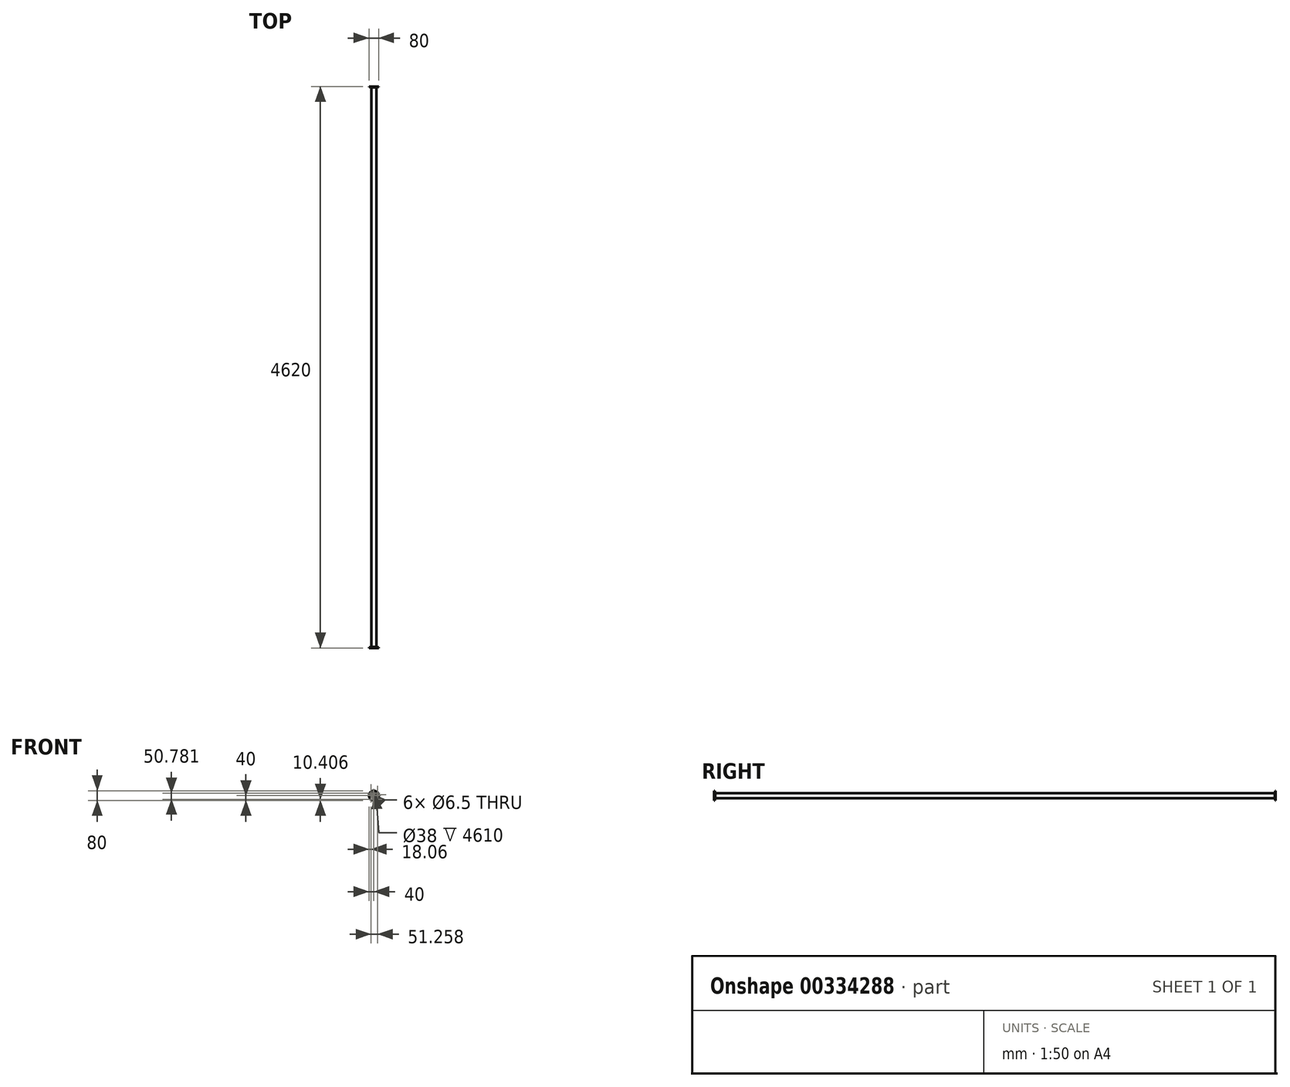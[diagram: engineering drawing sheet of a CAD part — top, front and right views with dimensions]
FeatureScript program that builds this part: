
annotation { "Feature Type Name" : "Feature", "Feature Type Description" : "" }
export const myFeature = defineFeature(function(context is Context, id is Id, definition is map)
    precondition{}
    {
        {
            assignVariable(context, id + "F0", {"name" : "L", "anyValue" : 4620});
        }
        {
            assignVariable(context, id + "F1", {"name" : "Dicke", "anyValue" : 5});
        }
        {
            var Q0;
            Q0=qCreatedBy(makeId("Front.planeOp"),FACE);
            var sketch = newSketch(context, id + "F2", { "sketchPlane" : qUnion([Q0])});
            skCircle(sketch, "E0", {"center": v(0, 0) * mm, "radius": 21 * mm});
            skCircle(sketch, "E1", {"center": v(0, 0) * mm, "radius": 19 * mm});
            skSolve(sketch);
        }
        {
            var Q0;
            Q0=makeQuery(id+"F2.imprint","IMPRINT",FACE,{"disambiguationData":[TD([[makeQuery(id+"F2.imprint","IMPRINT",EDGE,{"derivedFrom":sQuery(id+"F2.wireOp",EDGE,"E0")}),1.0]])]});
            extrude(context, id + "F3", {"entities" : qUnion([Q0]), "depth" : (getVariable(context, 'L')) * mm});
        }
        {
            var Q0;
            Q0=makeQuery(id+"F3.opExtrude","CAP_FACE",FACE,{"disambiguationData":[OSD([sQuery(id+"F2.wireOp",EDGE,"E0"),sQuery(id+"F2.wireOp",EDGE,"E1")])],"isStart":false});
            var sketch = newSketch(context, id + "F4", { "sketchPlane" : qUnion([Q0])});
            skCircle(sketch, "E2", {"center": v(0, 0) * mm, "radius": 40 * mm});
            skLineSegment(sketch, "E3", {"start": v(-47.57, 0) * mm, "end": v(49.17, 0) * mm, "construction": true});
            skLineSegment(sketch, "E4", {"start": v(-47.96, -13.75) * mm, "end": v(52.41, 15.03) * mm, "construction": true});
            skCircle(sketch, "E5", {"center": v(29.32, 8.4) * mm, "radius": 3.25 * mm});
            skCircle(sketch, "E6", {"center": v(-29.32, -8.4) * mm, "radius": 3.25 * mm, "construction": true});
            skPoint(sketch, "E7", {"position": v(20.19, 5.79) * mm});
            skPoint(sketch, "E8", {"position": v(38.45, 11.03) * mm});
            skLineSegment(sketch, "E9", {"start": v(22.92, 30.73) * mm, "end": v(29.32, 8.4) * mm, "construction": true});
            skLineSegment(sketch, "E10", {"start": v(-29.32, -8.4) * mm, "end": v(0, -110.65) * mm, "construction": true});
            skPoint(sketch, "E11", {"position": v(-20.19, -5.79) * mm});
            skPoint(sketch, "E12", {"position": v(-38.45, -11.03) * mm});
            skPoint(sketch, "E13", {"position": v(-49.5, 13.38) * mm});
            skCircle(sketch, "E14.1.0", {"center": v(-21.94, 21.19) * mm, "radius": 3.25 * mm});
            skCircle(sketch, "E14.2.0", {"center": v(-7.38, -29.6) * mm, "radius": 3.25 * mm});
            skSolve(sketch);
        }
        {
            var Q0;
            Q0=makeQuery(id+"F4.imprint","IMPRINT",FACE,{"disambiguationData":[TD([[makeQuery(id+"F4.imprint","IMPRINT",EDGE,{"derivedFrom":sQuery(id+"F4.wireOp",EDGE,"E2")}),1.0]])]});
            var Q1;
            Q1=makeQuery(id+"F4.imprint","IMPRINT",FACE,{"disambiguationData":[TD([[makeQuery(id+"F4.imprint","IMPRINT",EDGE,{"derivedFrom":makeQuery(id+"F3.opExtrude","CAP_EDGE",EDGE,{"disambiguationData":[OSD([sQuery(id+"F2.wireOp",EDGE,"E1")])],"isStart":false})}),1.0]])]});
            var Q2;
            Q2=makeQuery(id+"F4.imprint","IMPRINT",FACE,{"disambiguationData":[TD([[makeQuery(id+"F4.imprint","IMPRINT",EDGE,{"derivedFrom":makeQuery(id+"F3.opExtrude","CAP_EDGE",EDGE,{"disambiguationData":[OSD([sQuery(id+"F2.wireOp",EDGE,"E0")])],"isStart":false})}),1.0]])]});
            extrude(context, id + "F5", {"entities" : qUnion([Q0, Q1, Q2]), "operationType" : NewBodyOperationType.ADD, "oppositeDirection" : true, "depth" : (getVariable(context, 'Dicke')) * mm});
        }
        {
            var Q0;
            Q0=qSketchRegion(id+"F4",true);
            extrude(context, id + "F6", {"entities" : qUnion([Q0]), "operationType" : NewBodyOperationType.ADD, "oppositeDirection" : true, "depth" : (getVariable(context, 'L')) * mm, "hasSecondDirection" : true, "secondDirectionOppositeDirection" : true, "secondDirectionDepth" : (getVariable(context, 'L') - getVariable(context, 'Dicke')) * mm});
        }
        {
            var Q0;
            Q0=makeQuery(id+"F5.opExtrude","CAP_EDGE",EDGE,{"disambiguationData":[OSD([sQuery(id+"F4.wireOp",EDGE,"E5")])],"isStart":false});
            var Q1;
            Q1=makeQuery(id+"F5.opExtrude","CAP_EDGE",EDGE,{"disambiguationData":[OSD([sQuery(id+"F4.wireOp",EDGE,"E14.1.0")])],"isStart":false});
            var Q2;
            Q2=makeQuery(id+"F5.opExtrude","CAP_EDGE",EDGE,{"disambiguationData":[OSD([sQuery(id+"F4.wireOp",EDGE,"E14.2.0")])],"isStart":false});
            var Q3;
            Q3=makeQuery(id+"F6.opExtrude","CAP_EDGE",EDGE,{"disambiguationData":[OSD([sQuery(id+"F4.wireOp",EDGE,"E14.2.0")])],"isStart":true});
            var Q4;
            Q4=makeQuery(id+"F6.opExtrude","CAP_EDGE",EDGE,{"disambiguationData":[OSD([sQuery(id+"F4.wireOp",EDGE,"E5")])],"isStart":true});
            var Q5;
            Q5=makeQuery(id+"F6.opExtrude","CAP_EDGE",EDGE,{"disambiguationData":[OSD([sQuery(id+"F4.wireOp",EDGE,"E14.1.0")])],"isStart":true});
            chamfer(context, id + "F7", {"entities" : qUnion([Q0, Q1, Q2, Q3, Q4, Q5]), "width" : 2 * mm, "tangentPropagation" : true});
        }
        {
            var Q0;
            Q0=makeQuery(id+"F6.boolean.opBoolean","INTERSECT",EDGE,{"derivedFrom":[makeQuery(id+"F3.opExtrude","SWEPT_FACE",FACE,{"disambiguationData":[OSD([sQuery(id+"F2.wireOp",EDGE,"E0")])]}),makeQuery(id+"F6.opExtrude","CAP_FACE",FACE,{"disambiguationData":[OSD([sQuery(id+"F4.wireOp",EDGE,"E2"),sQuery(id+"F4.wireOp",EDGE,"E5"),sQuery(id+"F4.wireOp",EDGE,"E14.1.0"),sQuery(id+"F4.wireOp",EDGE,"E14.2.0")])],"isStart":true})]});
            var Q1;
            Q1=makeQuery(id+"F5.boolean.opBoolean","INTERSECT",EDGE,{"derivedFrom":[makeQuery(id+"F3.opExtrude","SWEPT_FACE",FACE,{"disambiguationData":[OSD([sQuery(id+"F2.wireOp",EDGE,"E0")])]}),makeQuery(id+"F5.opExtrude","CAP_FACE",FACE,{"disambiguationData":[OSD([sQuery(id+"F4.wireOp",EDGE,"E2"),sQuery(id+"F4.wireOp",EDGE,"E5"),sQuery(id+"F4.wireOp",EDGE,"E14.1.0"),sQuery(id+"F4.wireOp",EDGE,"E14.2.0")])],"isStart":false})]});
            chamfer(context, id + "F8", {"entities" : qUnion([Q0, Q1]), "width" : 3 * mm, "tangentPropagation" : true});
        }
    });
